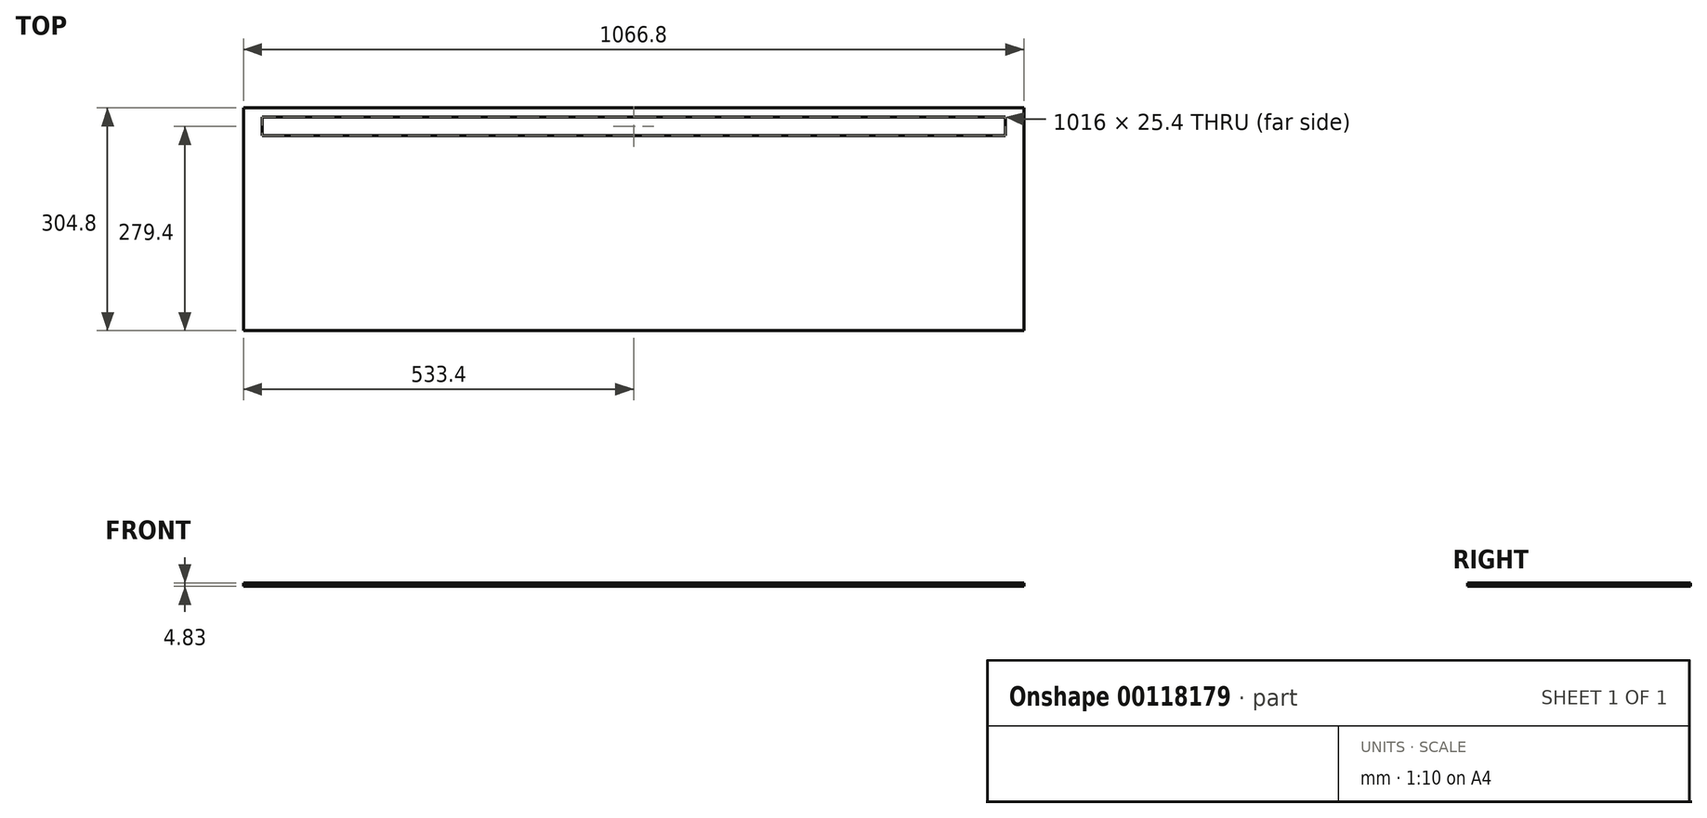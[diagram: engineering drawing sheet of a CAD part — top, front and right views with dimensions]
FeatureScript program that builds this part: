
annotation { "Feature Type Name" : "Feature", "Feature Type Description" : "" }
export const myFeature = defineFeature(function(context is Context, id is Id, definition is map)
    precondition{}
    {
        {
            var Q0;
            Q0=qCreatedBy(makeId("Top.planeOp"),FACE);
            var sketch = newSketch(context, id + "F0", { "sketchPlane" : qUnion([Q0])});
            skLineSegment(sketch, "E0.bottom", {"start": v(533.4, 152.4) * mm, "end": v(-533.4, 152.4) * mm});
            skLineSegment(sketch, "E0.top", {"start": v(533.4, -152.4) * mm, "end": v(-533.4, -152.4) * mm});
            skLineSegment(sketch, "E0.left", {"start": v(533.4, 152.4) * mm, "end": v(533.4, -152.4) * mm});
            skLineSegment(sketch, "E0.right", {"start": v(-533.4, 152.4) * mm, "end": v(-533.4, -152.4) * mm});
            skPoint(sketch, "E0.middle", {"position": v(0, 0) * mm});
            skSolve(sketch);
        }
        {
            var Q0;
            Q0=makeQuery(id+"F0.imprint","IMPRINT",FACE,{"disambiguationData":[TD([[makeQuery(id+"F0.imprint","IMPRINT",EDGE,{"derivedFrom":sQuery(id+"F0.wireOp",EDGE,"E0.bottom")}),1.0]])]});
            extrude(context, id + "F1", {"entities" : qUnion([Q0]), "depth" : 4.83 * mm});
        }
        {
            var Q0;
            Q0=makeQuery(id+"F1.opExtrude","CAP_FACE",FACE,{"disambiguationData":[OSD([sQuery(id+"F0.wireOp",EDGE,"E0.bottom"),sQuery(id+"F0.wireOp",EDGE,"E0.top"),sQuery(id+"F0.wireOp",EDGE,"E0.left"),sQuery(id+"F0.wireOp",EDGE,"E0.right")])],"isStart":false});
            var sketch = newSketch(context, id + "F2", { "sketchPlane" : qUnion([Q0])});
            skLineSegment(sketch, "E1.bottom", {"start": v(508, 139.7) * mm, "end": v(-508, 139.7) * mm});
            skLineSegment(sketch, "E1.top", {"start": v(508, 114.3) * mm, "end": v(-508, 114.3) * mm});
            skLineSegment(sketch, "E1.left", {"start": v(508, 139.7) * mm, "end": v(508, 114.3) * mm});
            skLineSegment(sketch, "E1.right", {"start": v(-508, 139.7) * mm, "end": v(-508, 114.3) * mm});
            skPoint(sketch, "E1.middle", {"position": v(0, 127) * mm});
            skSolve(sketch);
        }
        {
            var Q0;
            Q0 = qSketchRegion(id + "F2", true);
            var Q1;
            Q1=makeQuery(id+"F1.opExtrude","CAP_FACE",FACE,{"disambiguationData":[OSD([sQuery(id+"F0.wireOp",EDGE,"E0.bottom"),sQuery(id+"F0.wireOp",EDGE,"E0.top"),sQuery(id+"F0.wireOp",EDGE,"E0.left"),sQuery(id+"F0.wireOp",EDGE,"E0.right")])],"isStart":true});
            extrude(context, id + "F3", {"entities" : qUnion([Q0]), "operationType" : NewBodyOperationType.REMOVE, "endBound" : BoundingType.UP_TO_SURFACE, "oppositeDirection" : true, "endBoundEntityFace" : qUnion([Q1]), "depth" : 25.4 * mm});
        }
    });
